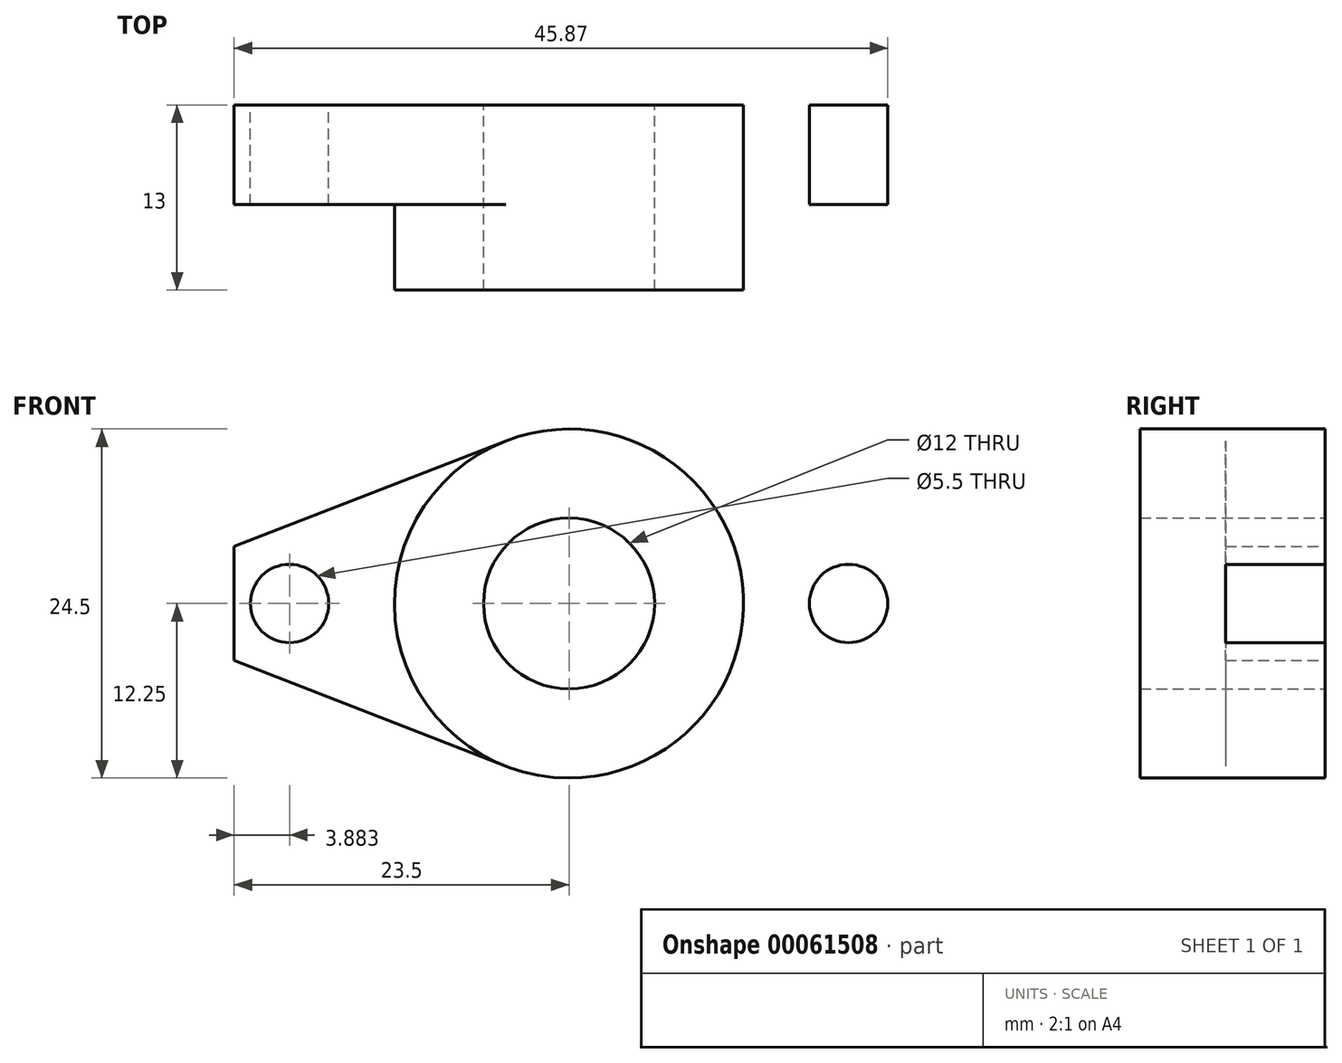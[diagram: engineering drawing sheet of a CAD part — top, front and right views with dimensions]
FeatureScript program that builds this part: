
annotation { "Feature Type Name" : "Feature", "Feature Type Description" : "" }
export const myFeature = defineFeature(function(context is Context, id is Id, definition is map)
    precondition{}
    {
        {
            var Q0;
            Q0=qCreatedBy(makeId("Front.planeOp"),FACE);
            var sketch = newSketch(context, id + "F0", { "sketchPlane" : qUnion([Q0])});
            skCircle(sketch, "E0", {"center": v(0, 0) * mm, "radius": 6 * mm});
            skCircle(sketch, "E1", {"center": v(-19.62, 0) * mm, "radius": 2.75 * mm});
            skCircle(sketch, "E2", {"center": v(0, 0) * mm, "radius": 12.25 * mm});
            skCircle(sketch, "E3.MirrorC", {"center": v(19.62, 0) * mm, "radius": 2.75 * mm});
            skLineSegment(sketch, "E4", {"start": v(-23.5, 0) * mm, "end": v(-23.5, 4) * mm});
            skLineSegment(sketch, "E5.MirrorCS", {"start": v(-23.5, 0) * mm, "end": v(-23.5, -4) * mm});
            skLineSegment(sketch, "E6.MirrorCS", {"start": v(23.5, 0) * mm, "end": v(23.5, 4) * mm});
            skLineSegment(sketch, "E7.MirrorCS", {"start": v(23.5, 0) * mm, "end": v(23.5, -4) * mm});
            skLineSegment(sketch, "E8", {"start": v(-23.5, -4) * mm, "end": v(-4.44, -11.42) * mm});
            skLineSegment(sketch, "E9.MirrorCS", {"start": v(-23.5, 4) * mm, "end": v(-4.44, 11.42) * mm});
            skLineSegment(sketch, "E10.MirrorCS", {"start": v(23.5, 4) * mm, "end": v(4.44, 11.42) * mm});
            skLineSegment(sketch, "E11.MirrorCS", {"start": v(23.5, -4) * mm, "end": v(4.44, -11.42) * mm});
            skSolve(sketch);
        }
        {
            var Q0;
            Q0=makeQuery(id+"F0.imprint","IMPRINT",FACE,{"disambiguationData":[TD([[makeQuery(id+"F0.imprint","IMPRINT",EDGE,{"derivedFrom":sQuery(id+"F0.wireOp",EDGE,"E0")}),-1.0]])]});
            extrude(context, id + "F1", {"entities" : qUnion([Q0]), "depth" : 13 * mm});
        }
        {
            var Q0;
            Q0=makeQuery(id+"F0.imprint","IMPRINT",FACE,{"disambiguationData":[TD([[makeQuery(id+"F0.imprint","IMPRINT",EDGE,{"derivedFrom":sQuery(id+"F0.wireOp",EDGE,"E1")}),-1.0]])]});
            var Q1;
            Q1=makeQuery(id+"F0.imprint","IMPRINT",FACE,{"disambiguationData":[TD([[makeQuery(id+"F0.imprint","IMPRINT",EDGE,{"derivedFrom":sQuery(id+"F0.wireOp",EDGE,"E3.MirrorC")}),1.0]])]});
            extrude(context, id + "F2", {"entities" : qUnion([Q0, Q1]), "operationType" : NewBodyOperationType.ADD, "depth" : 7 * mm});
        }
    });
